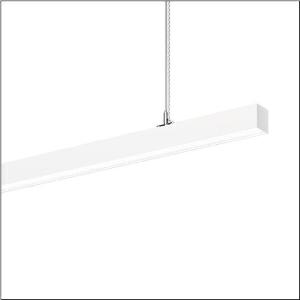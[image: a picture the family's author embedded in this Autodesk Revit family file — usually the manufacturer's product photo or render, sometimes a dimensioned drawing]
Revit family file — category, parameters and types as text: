
# Revit family: silica_r__21_51mx30dc39wb_5262
name_source: partatom
category: Lighting Fixtures
units: mm (PartAtom-declared; Revit-internal decimal feet)

## family parameters
Cut with Voids When Loaded = No
Host = Face
Light Source = No
Part Type = Normal
Room Calculation Point = No
Round Connector Dimension = Use Diameter
Shared = No

## types (1)
- --- (1 x LED, 10520 lm, 68.3 W, 3000K)
    Apparent Load = 68 VA
    CIE Flux Codes = 47 79 96 57 100
    Color Rendering = 80
    Color Temperature = 3000K
    Default Elevation = 1800 mm
    Description = Silica® 21, office luminaire, primary optical cover: cover, of PMMA, opal, light emission: direct/indirect distribution, primary light characteristic: symmetric, installation type: suspended mounting, LED, rated luminous flux: 10.520lm, luminous efficacy: 154lm/W, light colour: 830, colour temperature: 3000K, with terminal, 3+2-pole, max. 2.5mm², mains connection: 220..240V, AC, 50/60Hz, rated input power: 68.3W, luminaire housing, of aluminium, traffic white (RAL 9016), length: 3.004mm, width: 53mm, height: 53mm, protection rating (complete): IP20, insulation class (complete): insulation class I (protective earthing), certification: CE, permissible operating ambient temperature: 0..+35°C, standard: EN 50419, packaging unit: 1 piece
    Height = 53 mm
    Lamp = 1 x LED
    Lamp Light Flux = 10520 lm
    Lamp Power = 68.3 W
    Lamp count = 1
    Length = 3004 mm
    Luminous efficacy = 154 lm/W
    Manufacturer = Siteco
    ModVariant = No
    Model = 51MX30DC39WB
    Mounting Place = Ceiling
    Mounting Type = Pendant
    Number of Poles = 1
    OnlyDefault = Yes
    Power Factor = 1
    Product Name = Silica® 21
    Product group = office luminaire | ceiling pendant
    ProductGroupID = 902
    Protection Class = Protection class I
    Protection Degree = IP 20
    RLX_Detail_Level = 1
    RLX_Emergency_Light_Flux = 0 lm
    RLX_Emergency_Type = 0
    RLX_Emergency_Type_DB = No
    RlxData = <blob elided: 21365 chars, md5=a1614267>
    Socket = socket
    Standby Power = 0 W
    System Light Flux = 10520 lm
    System Power = 68 W
    Type Comments = factory setting: luminous flux: 100 % | dim-lin: 254 | 233 mA
    Type Image = l_1297784.jpg
    URL = http://relux.com
    VarID = @adj_047429
    Voltage = 0 V
    Weight = 0.00 kg
    Width = 53 mm

## geometry (parser evidence)
native form markers: Blend x4, Sweep x10
no freeform markers — native parametric forms only
